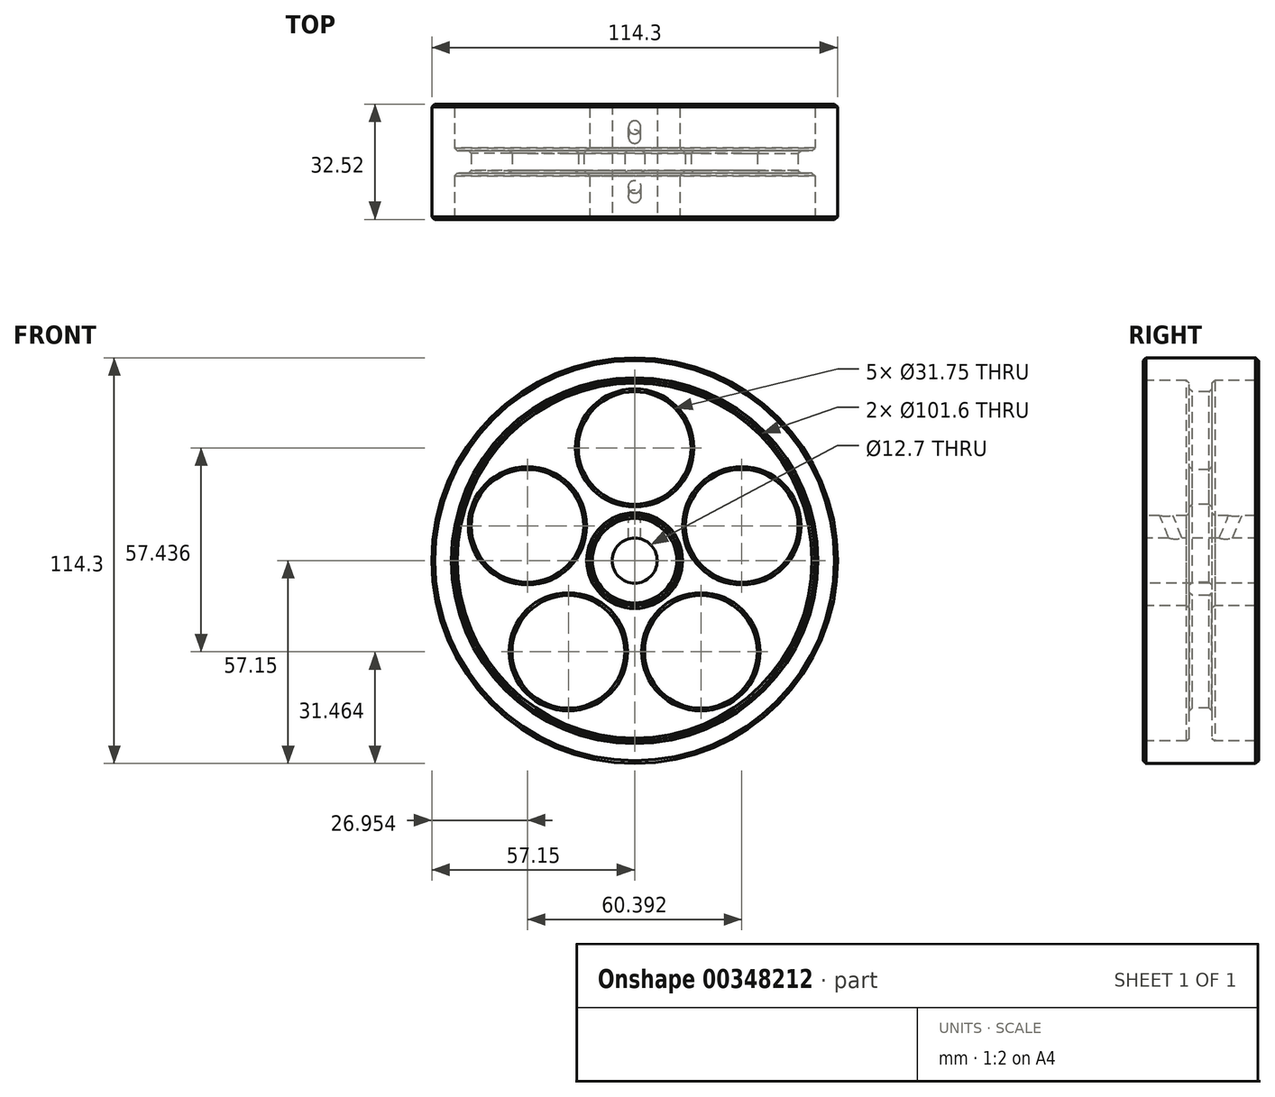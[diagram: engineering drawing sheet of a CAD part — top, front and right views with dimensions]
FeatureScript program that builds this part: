
annotation { "Feature Type Name" : "Feature", "Feature Type Description" : "" }
export const myFeature = defineFeature(function(context is Context, id is Id, definition is map)
    precondition{}
    {
        {
            var Q0;
            Q0=qCreatedBy(makeId("Right.planeOp"),FACE);
            var sketch = newSketch(context, id + "F0", { "sketchPlane" : qUnion([Q0])});
            skLineSegment(sketch, "E0", {"start": v(-16.26, 6.35) * mm, "end": v(-16.26, 12.7) * mm});
            skLineSegment(sketch, "E1", {"start": v(-16.26, 12.7) * mm, "end": v(-3.17, 12.7) * mm});
            skLineSegment(sketch, "E2", {"start": v(-3.17, 12.7) * mm, "end": v(-3.18, 50.8) * mm});
            skLineSegment(sketch, "E3", {"start": v(-3.18, 50.8) * mm, "end": v(-16.26, 50.8) * mm});
            skLineSegment(sketch, "E4", {"start": v(-16.26, 50.8) * mm, "end": v(-16.26, 57.15) * mm});
            skLineSegment(sketch, "E5", {"start": v(-16.26, 57.15) * mm, "end": v(16.26, 57.15) * mm});
            skLineSegment(sketch, "E6", {"start": v(16.26, 57.15) * mm, "end": v(16.26, 50.8) * mm});
            skLineSegment(sketch, "E7", {"start": v(16.26, 50.8) * mm, "end": v(3.17, 50.8) * mm});
            skLineSegment(sketch, "E8", {"start": v(3.17, 50.8) * mm, "end": v(3.18, 12.7) * mm});
            skLineSegment(sketch, "E9", {"start": v(3.18, 12.7) * mm, "end": v(16.26, 12.7) * mm});
            skLineSegment(sketch, "E10", {"start": v(16.26, 12.7) * mm, "end": v(16.26, 6.35) * mm});
            skLineSegment(sketch, "E11", {"start": v(16.26, 6.35) * mm, "end": v(-16.26, 6.35) * mm});
            skLineSegment(sketch, "E12", {"start": v(-16.39, 0) * mm, "end": v(18.55, 0) * mm, "construction": true});
            skPoint(sketch, "E13", {"position": v(0, 57.15) * mm});
            skPoint(sketch, "E14", {"position": v(-9.72, 12.7) * mm});
            skPoint(sketch, "E15", {"position": v(9.72, 12.7) * mm});
            skSolve(sketch);
        }
        {
            var Q0;
            Q0=qSketchRegion(id+"F0",true);
            var Q1;
            Q1=sQuery(id+"F0.wireOp",EDGE,"E12");
            revolve(context, id + "F1", {"entities" : qUnion([Q0]), "axis" : qUnion([Q1]), "revolveType" : RevolveType.FULL});
        }
        {
            var Q0;
            Q0=qCreatedBy(makeId("Front.planeOp"),FACE);
            var sketch = newSketch(context, id + "F2", { "sketchPlane" : qUnion([Q0])});
            skCircle(sketch, "E16", {"center": v(0, 31.75) * mm, "radius": 15.88 * mm});
            skCircle(sketch, "E17.1.0", {"center": v(-30.2, 9.81) * mm, "radius": 15.88 * mm});
            skCircle(sketch, "E17.2.0", {"center": v(-18.66, -25.69) * mm, "radius": 15.88 * mm});
            skCircle(sketch, "E17.3.0", {"center": v(18.66, -25.69) * mm, "radius": 15.88 * mm});
            skCircle(sketch, "E17.4.0", {"center": v(30.2, 9.81) * mm, "radius": 15.88 * mm});
            skPoint(sketch, "E17.center", {"position": v(0, 0) * mm});
            skCircle(sketch, "E18", {"center": v(0, 0) * mm, "radius": 31.75 * mm, "construction": true});
            skSolve(sketch);
        }
        {
            var Q0;
            Q0=qSketchRegion(id+"F2",true);
            extrude(context, id + "F3", {"entities" : qUnion([Q0]), "operationType" : NewBodyOperationType.REMOVE, "endBound" : BoundingType.SYMMETRIC, "oppositeDirection" : true, "depth" : 50.8 * mm});
        }
        {
            var Q0;
            Q0=qCreatedBy(makeId("Top.planeOp"),FACE);
            var sketch = newSketch(context, id + "F4", { "sketchPlane" : qUnion([Q0])});
            skLineSegment(sketch, "E19", {"start": v(-62.2, -50.8) * mm, "end": v(72.14, -50.8) * mm, "construction": true});
            skLineSegment(sketch, "E20", {"start": v(-62.2, 50.8) * mm, "end": v(72.14, 50.8) * mm, "construction": true});
            skSolve(sketch);
        }
        {
            var Q0;
            Q0=sQuery(id+"F4.wireOp",EDGE,"E19");
            cPlane(context, id + "F5", {"entities" : qUnion([Q0]), "cplaneType" : CPlaneType.LINE_ANGLE, "offset" : 152.4 * mm, "angle" : 292.5 * degree, "width" : 152.4 * mm, "height" : 152.4 * mm});
        }
        {
            var Q0;
            Q0=sQuery(id+"F4.wireOp",EDGE,"E20");
            cPlane(context, id + "F6", {"entities" : qUnion([Q0]), "cplaneType" : CPlaneType.LINE_ANGLE, "offset" : 152.4 * mm, "angle" : 67.5 * degree, "width" : 152.4 * mm, "height" : 152.4 * mm});
        }
        {
            var Q0;
            Q0=qCreatedBy(id+"F5.planeOp",FACE);
            var sketch = newSketch(context, id + "F7", { "sketchPlane" : qUnion([Q0])});
            skCircle(sketch, "E21", {"center": v(0, 4.12) * mm, "radius": 1.73 * mm});
            skSolve(sketch);
        }
        {
            var Q0;
            Q0=qSketchRegion(id+"F7",true);
            var Q1;
            Q1=makeQuery(id+"F1.opRevolve","SWEPT_FACE",FACE,{"disambiguationData":[OSD([sQuery(id+"F0.wireOp",EDGE,"E11")])]});
            extrude(context, id + "F8", {"entities" : qUnion([Q0]), "operationType" : NewBodyOperationType.REMOVE, "endBound" : BoundingType.UP_TO_SURFACE, "endBoundEntityFace" : qUnion([Q1]), "depth" : 25.4 * mm});
        }
        {
            var Q0;
            Q0=qCreatedBy(id+"F6.planeOp",FACE);
            var sketch = newSketch(context, id + "F9", { "sketchPlane" : qUnion([Q0])});
            skCircle(sketch, "E22", {"center": v(0, 4.12) * mm, "radius": 1.73 * mm});
            skSolve(sketch);
        }
        {
            var Q0;
            Q0=qSketchRegion(id+"F9",true);
            var Q1;
            Q1=makeQuery(id+"F1.opRevolve","SWEPT_FACE",FACE,{"disambiguationData":[OSD([sQuery(id+"F0.wireOp",EDGE,"E11")])]});
            extrude(context, id + "F10", {"entities" : qUnion([Q0]), "operationType" : NewBodyOperationType.REMOVE, "endBound" : BoundingType.UP_TO_SURFACE, "oppositeDirection" : true, "endBoundEntityFace" : qUnion([Q1]), "depth" : 25.4 * mm});
        }
        {
            var Q0;
            Q0=makeQuery(id+"F1.opRevolve","SWEPT_EDGE",EDGE,{"disambiguationData":[OSD([sQuery(id+"F0.wireOp",EDGE,"E4"),sQuery(id+"F0.wireOp",EDGE,"E5")])]});
            var Q1;
            Q1=makeQuery(id+"F1.opRevolve","SWEPT_EDGE",EDGE,{"disambiguationData":[OSD([sQuery(id+"F0.wireOp",EDGE,"E5"),sQuery(id+"F0.wireOp",EDGE,"E6")])]});
            var Q2;
            Q2=makeQuery(id+"F1.opRevolve","SWEPT_EDGE",EDGE,{"disambiguationData":[OSD([sQuery(id+"F0.wireOp",EDGE,"E3"),sQuery(id+"F0.wireOp",EDGE,"E4")])]});
            var Q3;
            Q3=makeQuery(id+"F1.opRevolve","SWEPT_EDGE",EDGE,{"disambiguationData":[OSD([sQuery(id+"F0.wireOp",EDGE,"E2"),sQuery(id+"F0.wireOp",EDGE,"E3")])]});
            var Q4;
            Q4=makeQuery(id+"F1.opRevolve","SWEPT_EDGE",EDGE,{"disambiguationData":[OSD([sQuery(id+"F0.wireOp",EDGE,"E6"),sQuery(id+"F0.wireOp",EDGE,"E7")])]});
            var Q5;
            Q5=makeQuery(id+"F1.opRevolve","SWEPT_EDGE",EDGE,{"disambiguationData":[OSD([sQuery(id+"F0.wireOp",EDGE,"E7"),sQuery(id+"F0.wireOp",EDGE,"E8")])]});
            var Q6;
            Q6=makeQuery(id+"F1.opRevolve","SWEPT_EDGE",EDGE,{"disambiguationData":[OSD([sQuery(id+"F0.wireOp",EDGE,"E9"),sQuery(id+"F0.wireOp",EDGE,"E10")])]});
            var Q7;
            Q7=makeQuery(id+"F1.opRevolve","SWEPT_EDGE",EDGE,{"disambiguationData":[OSD([sQuery(id+"F0.wireOp",EDGE,"E8"),sQuery(id+"F0.wireOp",EDGE,"E9")])]});
            var Q8;
            Q8=makeQuery(id+"F1.opRevolve","SWEPT_EDGE",EDGE,{"disambiguationData":[OSD([sQuery(id+"F0.wireOp",EDGE,"E0"),sQuery(id+"F0.wireOp",EDGE,"E1")])]});
            var Q9;
            Q9=makeQuery(id+"F1.opRevolve","SWEPT_EDGE",EDGE,{"disambiguationData":[OSD([sQuery(id+"F0.wireOp",EDGE,"E1"),sQuery(id+"F0.wireOp",EDGE,"E2")])]});
            var Q10;
            Q10=makeQuery(id+"F3.boolean.opBoolean","INTERSECT",EDGE,{"derivedFrom":[makeQuery(id+"F1.opRevolve","SWEPT_FACE",FACE,{"disambiguationData":[OSD([sQuery(id+"F0.wireOp",EDGE,"E2")])]}),makeQuery(id+"F3.opExtrude","SWEPT_FACE",FACE,{"disambiguationData":[OSD([sQuery(id+"F2.wireOp",EDGE,"E16")])]})]});
            var Q11;
            Q11=makeQuery(id+"F3.boolean.opBoolean","INTERSECT",EDGE,{"derivedFrom":[makeQuery(id+"F1.opRevolve","SWEPT_FACE",FACE,{"disambiguationData":[OSD([sQuery(id+"F0.wireOp",EDGE,"E2")])]}),makeQuery(id+"F3.opExtrude","SWEPT_FACE",FACE,{"disambiguationData":[OSD([sQuery(id+"F2.wireOp",EDGE,"E17.4.0")])]})]});
            var Q12;
            Q12=makeQuery(id+"F3.boolean.opBoolean","INTERSECT",EDGE,{"derivedFrom":[makeQuery(id+"F1.opRevolve","SWEPT_FACE",FACE,{"disambiguationData":[OSD([sQuery(id+"F0.wireOp",EDGE,"E2")])]}),makeQuery(id+"F3.opExtrude","SWEPT_FACE",FACE,{"disambiguationData":[OSD([sQuery(id+"F2.wireOp",EDGE,"E17.3.0")])]})]});
            var Q13;
            Q13=makeQuery(id+"F3.boolean.opBoolean","INTERSECT",EDGE,{"derivedFrom":[makeQuery(id+"F1.opRevolve","SWEPT_FACE",FACE,{"disambiguationData":[OSD([sQuery(id+"F0.wireOp",EDGE,"E2")])]}),makeQuery(id+"F3.opExtrude","SWEPT_FACE",FACE,{"disambiguationData":[OSD([sQuery(id+"F2.wireOp",EDGE,"E17.2.0")])]})]});
            var Q14;
            Q14=makeQuery(id+"F3.boolean.opBoolean","INTERSECT",EDGE,{"derivedFrom":[makeQuery(id+"F1.opRevolve","SWEPT_FACE",FACE,{"disambiguationData":[OSD([sQuery(id+"F0.wireOp",EDGE,"E2")])]}),makeQuery(id+"F3.opExtrude","SWEPT_FACE",FACE,{"disambiguationData":[OSD([sQuery(id+"F2.wireOp",EDGE,"E17.1.0")])]})]});
            var Q15;
            Q15=makeQuery(id+"F3.boolean.opBoolean","INTERSECT",EDGE,{"derivedFrom":[makeQuery(id+"F1.opRevolve","SWEPT_FACE",FACE,{"disambiguationData":[OSD([sQuery(id+"F0.wireOp",EDGE,"E8")])]}),makeQuery(id+"F3.opExtrude","SWEPT_FACE",FACE,{"disambiguationData":[OSD([sQuery(id+"F2.wireOp",EDGE,"E16")])]})]});
            var Q16;
            Q16=makeQuery(id+"F3.boolean.opBoolean","INTERSECT",EDGE,{"derivedFrom":[makeQuery(id+"F1.opRevolve","SWEPT_FACE",FACE,{"disambiguationData":[OSD([sQuery(id+"F0.wireOp",EDGE,"E8")])]}),makeQuery(id+"F3.opExtrude","SWEPT_FACE",FACE,{"disambiguationData":[OSD([sQuery(id+"F2.wireOp",EDGE,"E17.1.0")])]})]});
            var Q17;
            Q17=makeQuery(id+"F3.boolean.opBoolean","INTERSECT",EDGE,{"derivedFrom":[makeQuery(id+"F1.opRevolve","SWEPT_FACE",FACE,{"disambiguationData":[OSD([sQuery(id+"F0.wireOp",EDGE,"E8")])]}),makeQuery(id+"F3.opExtrude","SWEPT_FACE",FACE,{"disambiguationData":[OSD([sQuery(id+"F2.wireOp",EDGE,"E17.2.0")])]})]});
            var Q18;
            Q18=makeQuery(id+"F3.boolean.opBoolean","INTERSECT",EDGE,{"derivedFrom":[makeQuery(id+"F1.opRevolve","SWEPT_FACE",FACE,{"disambiguationData":[OSD([sQuery(id+"F0.wireOp",EDGE,"E8")])]}),makeQuery(id+"F3.opExtrude","SWEPT_FACE",FACE,{"disambiguationData":[OSD([sQuery(id+"F2.wireOp",EDGE,"E17.3.0")])]})]});
            var Q19;
            Q19=makeQuery(id+"F3.boolean.opBoolean","INTERSECT",EDGE,{"derivedFrom":[makeQuery(id+"F1.opRevolve","SWEPT_FACE",FACE,{"disambiguationData":[OSD([sQuery(id+"F0.wireOp",EDGE,"E8")])]}),makeQuery(id+"F3.opExtrude","SWEPT_FACE",FACE,{"disambiguationData":[OSD([sQuery(id+"F2.wireOp",EDGE,"E17.4.0")])]})]});
            chamfer(context, id + "F11", {"entities" : qUnion([Q0, Q1, Q2, Q3, Q4, Q5, Q6, Q7, Q8, Q9, Q10, Q11, Q12, Q13, Q14, Q15, Q16, Q17, Q18, Q19]), "width" : 0.8 * mm, "tangentPropagation" : true});
        }
    });
